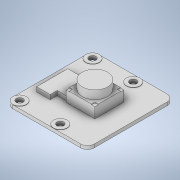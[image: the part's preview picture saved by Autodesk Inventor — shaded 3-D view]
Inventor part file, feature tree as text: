
AUTODESK INVENTOR PART (.ipt)
format: ipt  version: 2022 (Build 260153000, 153)  size: 220,160 bytes
history: native  units: mm
features: extrude x7, sketch x4, other x1, fillet x1, mirror x1, pattern_linear x1
ambient origin geometry x8: Origin, YZ Plane, XZ Plane, XY Plane, X Axis, Y Axis, Z Axis, Center Point
bodies: Body1 (feature_tree)
feature tree (15):
  other  "솔리드1"
  sketch  "스케치1"
  extrude  "돌출1"  Depth=25.5mm
  extrude  "돌출2"  Depth=24.0mm
  extrude  "돌출3"  Depth=8.5mm
  extrude  "돌출4"  Depth=8.5mm
  fillet  "모깎기1"  Radius=17.7mm
  mirror  "미러3"
  pattern_linear  "직사각형 패턴1"  Spacing1=1.0mm  [1 undecoded]
  sketch  "스케치2"
  sketch  "스케치3"
  extrude  "돌출5"  Depth=7.1mm
  extrude  "돌출6"  Depth=4.0mm
  extrude  "돌출7"  Depth=7.0mm
  sketch  "스케치4"
note: 1 required parameter value undecoded (feature->parameter linkage not recoverable at this tier; creation-order binding heuristic only, values carry confidence <= 0.55)
